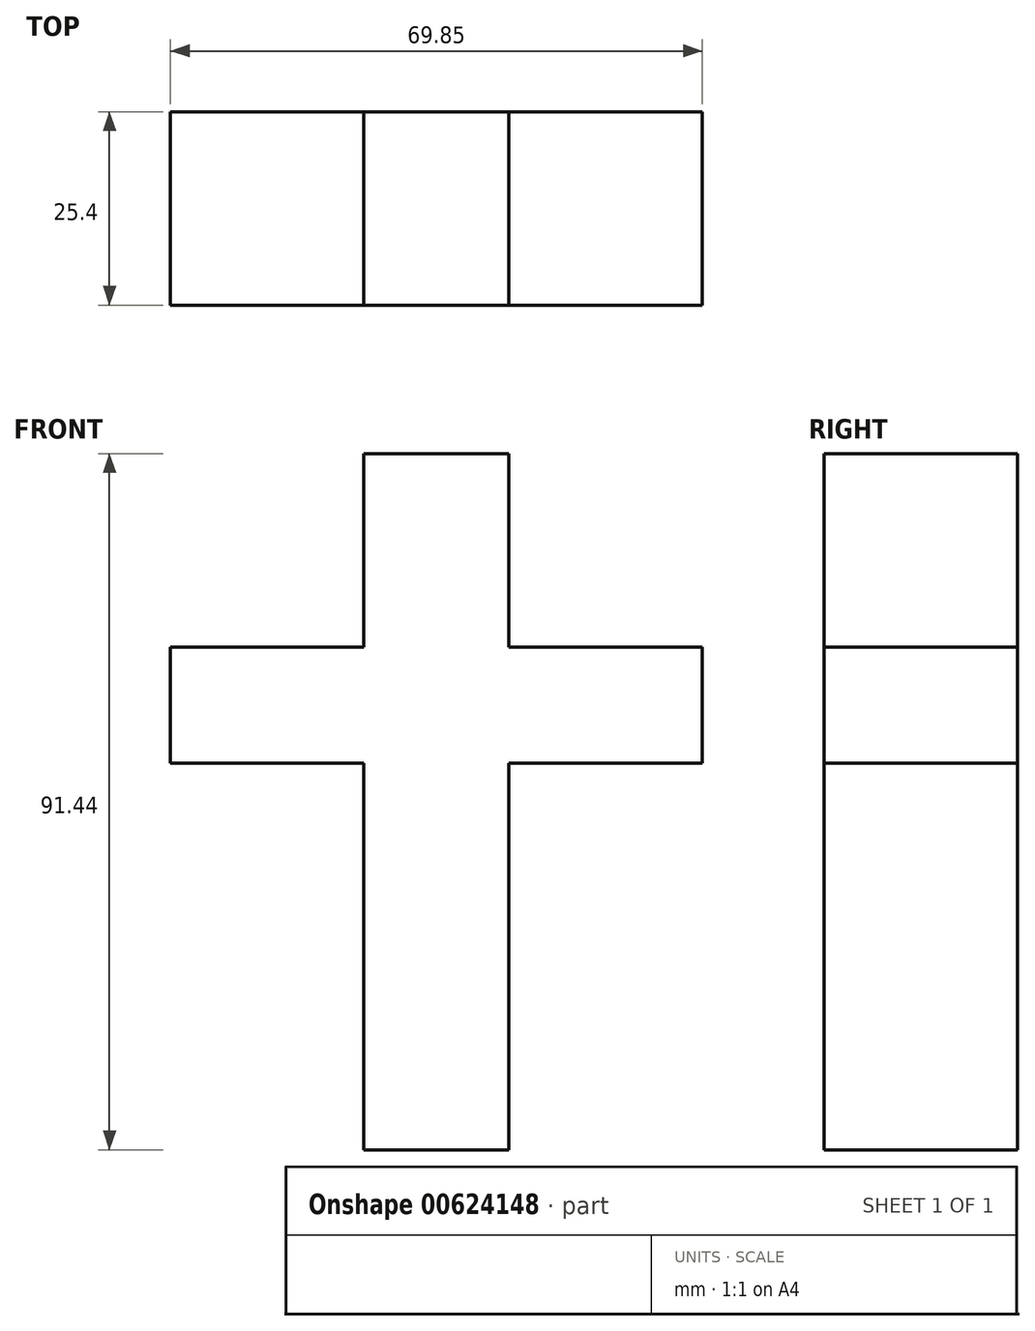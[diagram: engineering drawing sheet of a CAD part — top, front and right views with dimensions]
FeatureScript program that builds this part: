
annotation { "Feature Type Name" : "Feature", "Feature Type Description" : "" }
export const myFeature = defineFeature(function(context is Context, id is Id, definition is map)
    precondition{}
    {
        {
            var Q0;
            Q0=qCreatedBy(makeId("Front.planeOp"),FACE);
            var sketch = newSketch(context, id + "F0", { "sketchPlane" : qUnion([Q0])});
            skLineSegment(sketch, "E0", {"start": v(0, 0) * mm, "end": v(-25.4, 0) * mm});
            skLineSegment(sketch, "E1", {"start": v(-25.4, 0) * mm, "end": v(-25.4, 15.24) * mm});
            skLineSegment(sketch, "E2", {"start": v(-25.4, 15.24) * mm, "end": v(0, 15.24) * mm});
            skLineSegment(sketch, "E3", {"start": v(0, 15.24) * mm, "end": v(0, 40.64) * mm});
            skLineSegment(sketch, "E4", {"start": v(0, 40.64) * mm, "end": v(19.05, 40.64) * mm});
            skLineSegment(sketch, "E5", {"start": v(19.05, 40.64) * mm, "end": v(19.05, 15.24) * mm});
            skLineSegment(sketch, "E6", {"start": v(19.05, 15.24) * mm, "end": v(44.45, 15.24) * mm});
            skLineSegment(sketch, "E7", {"start": v(44.45, 15.24) * mm, "end": v(44.45, 0) * mm});
            skLineSegment(sketch, "E8", {"start": v(44.45, 0) * mm, "end": v(19.05, 0) * mm});
            skLineSegment(sketch, "E9", {"start": v(19.05, 0) * mm, "end": v(19.05, -50.8) * mm});
            skLineSegment(sketch, "E10", {"start": v(19.05, -50.8) * mm, "end": v(0, -50.8) * mm});
            skLineSegment(sketch, "E11", {"start": v(0, -50.8) * mm, "end": v(0, 0) * mm});
            skSolve(sketch);
        }
        {
            var Q0;
            Q0 = qSketchRegion(id + "F0", true);
            extrude(context, id + "F1", {"entities" : qUnion([Q0]), "depth" : 25.4 * mm, "offsetDistance" : 25.4 * mm});
        }
    });
